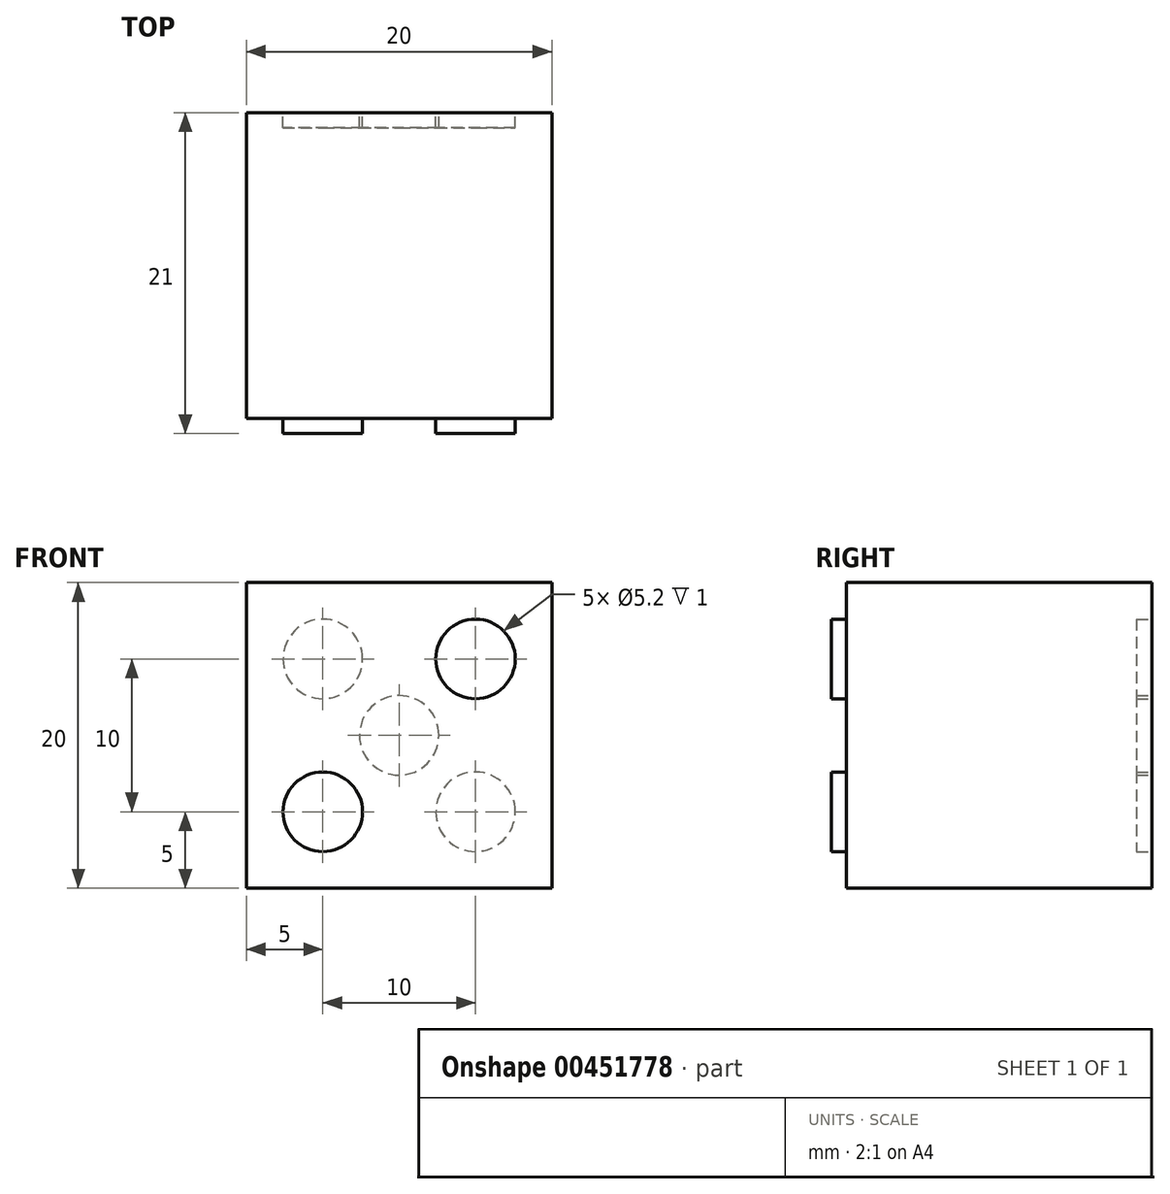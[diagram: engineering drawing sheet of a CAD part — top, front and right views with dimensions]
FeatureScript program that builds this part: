
annotation { "Feature Type Name" : "Feature", "Feature Type Description" : "" }
export const myFeature = defineFeature(function(context is Context, id is Id, definition is map)
    precondition{}
    {
        {
            var Q0;
            Q0=qCreatedBy(makeId("Front.planeOp"),FACE);
            var sketch = newSketch(context, id + "F0", { "sketchPlane" : qUnion([Q0])});
            skLineSegment(sketch, "E0.bottom", {"start": v(0, 0) * mm, "end": v(-20, 0) * mm});
            skLineSegment(sketch, "E0.top", {"start": v(0, 20) * mm, "end": v(-20, 20) * mm});
            skLineSegment(sketch, "E0.left", {"start": v(0, 0) * mm, "end": v(0, 20) * mm});
            skLineSegment(sketch, "E0.right", {"start": v(-20, 0) * mm, "end": v(-20, 20) * mm});
            skSolve(sketch);
        }
        {
            var Q0;
            Q0=makeQuery(id+"F0.imprint","IMPRINT",FACE,{"disambiguationData":[TD([[makeQuery(id+"F0.imprint","IMPRINT",EDGE,{"derivedFrom":sQuery(id+"F0.wireOp",EDGE,"E0.bottom")}),-1.0]])]});
            extrude(context, id + "F1", {"entities" : qUnion([Q0]), "depth" : 20 * mm});
        }
        {
            var Q0;
            Q0=makeQuery(id+"F1.opExtrude","CAP_FACE",FACE,{"disambiguationData":[OSD([sQuery(id+"F0.wireOp",EDGE,"E0.bottom"),sQuery(id+"F0.wireOp",EDGE,"E0.top"),sQuery(id+"F0.wireOp",EDGE,"E0.left"),sQuery(id+"F0.wireOp",EDGE,"E0.right")])],"isStart":true});
            var sketch = newSketch(context, id + "F2", { "sketchPlane" : qUnion([Q0])});
            skLineSegment(sketch, "E1", {"start": v(0, 20) * mm, "end": v(20, 0) * mm, "construction": true});
            skLineSegment(sketch, "E2", {"start": v(0, 0) * mm, "end": v(20, 20) * mm, "construction": true});
            skLineSegment(sketch, "E3", {"start": v(10, 0) * mm, "end": v(10, 20) * mm, "construction": true});
            skLineSegment(sketch, "E4", {"start": v(0, 10) * mm, "end": v(20, 10) * mm, "construction": true});
            skCircle(sketch, "E5", {"center": v(10, 10) * mm, "radius": 2.6 * mm});
            skCircle(sketch, "E6", {"center": v(5, 15) * mm, "radius": 2.6 * mm});
            skCircle(sketch, "E7.MirrorC", {"center": v(5, 5) * mm, "radius": 2.6 * mm});
            skCircle(sketch, "E8.MirrorC", {"center": v(15, 15) * mm, "radius": 2.6 * mm});
            skCircle(sketch, "E9.MirrorC", {"center": v(15, 5) * mm, "radius": 2.6 * mm});
            skSolve(sketch);
        }
        {
            var Q0;
            Q0 = qSketchRegion(id + "F2", true);
            extrude(context, id + "F3", {"entities" : qUnion([Q0]), "operationType" : NewBodyOperationType.REMOVE, "oppositeDirection" : true, "depth" : 1 * mm});
        }
        {
            var Q0;
            Q0=makeQuery(id+"F1.opExtrude","CAP_FACE",FACE,{"disambiguationData":[OSD([sQuery(id+"F0.wireOp",EDGE,"E0.bottom"),sQuery(id+"F0.wireOp",EDGE,"E0.top"),sQuery(id+"F0.wireOp",EDGE,"E0.left"),sQuery(id+"F0.wireOp",EDGE,"E0.right")])],"isStart":false});
            var sketch = newSketch(context, id + "F4", { "sketchPlane" : qUnion([Q0])});
            skLineSegment(sketch, "E10", {"start": v(-20, 20) * mm, "end": v(0, 0) * mm, "construction": true});
            skCircle(sketch, "E11", {"center": v(-5, 15) * mm, "radius": 2.6 * mm});
            skCircle(sketch, "E12.MirrorC", {"center": v(-15, 5) * mm, "radius": 2.6 * mm});
            skSolve(sketch);
        }
        {
            var Q0;
            Q0 = qSketchRegion(id + "F4", true);
            extrude(context, id + "F5", {"entities" : qUnion([Q0]), "operationType" : NewBodyOperationType.ADD, "depth" : 1 * mm});
        }
    });
